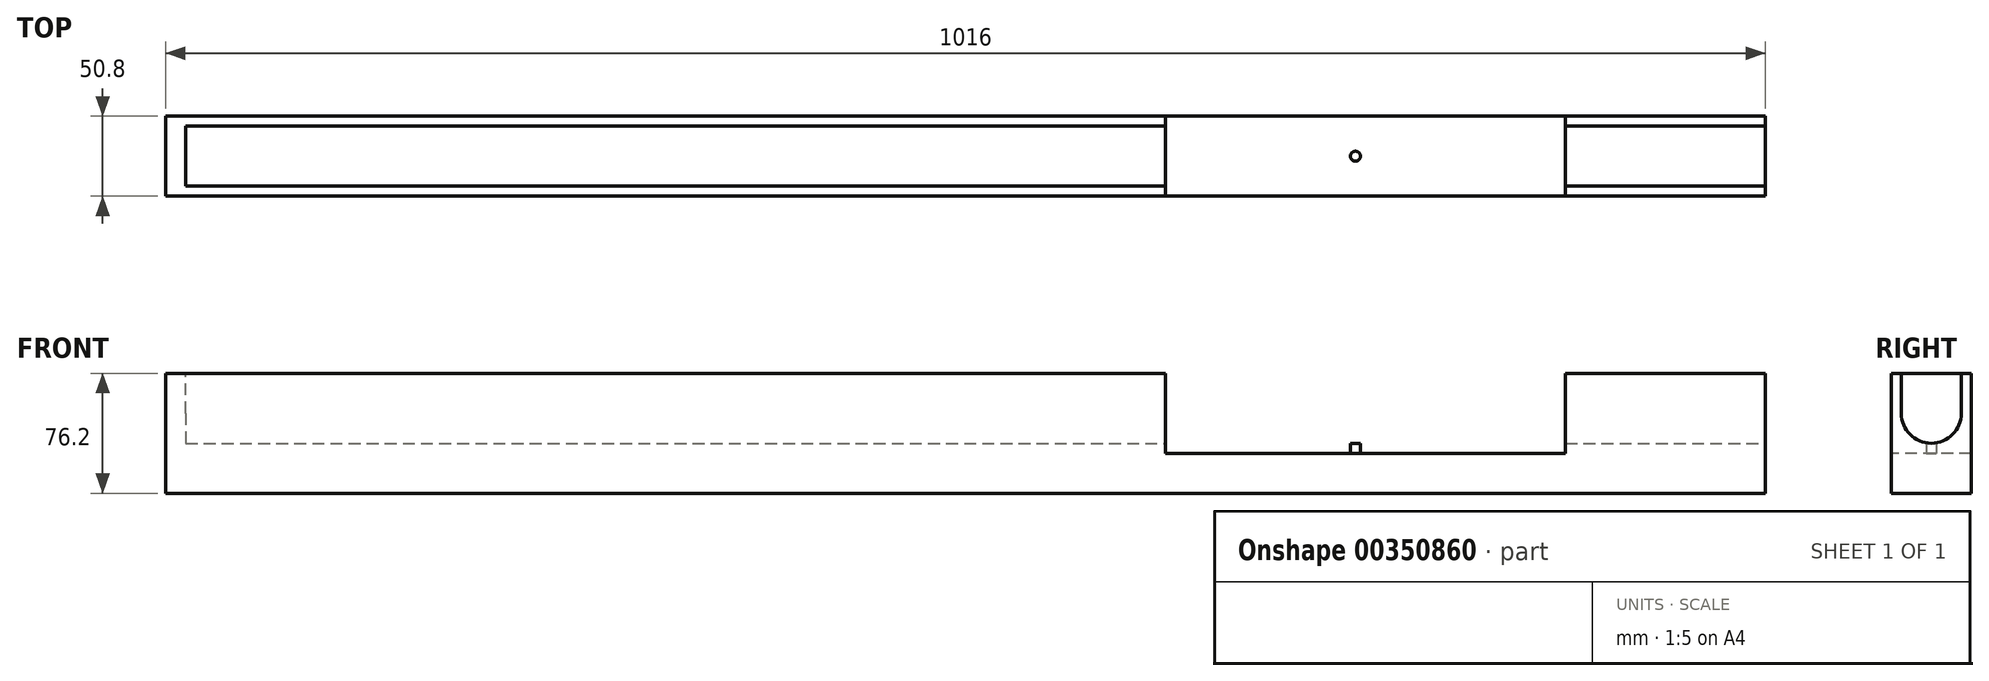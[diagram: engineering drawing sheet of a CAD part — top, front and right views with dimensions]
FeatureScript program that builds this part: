
annotation { "Feature Type Name" : "Feature", "Feature Type Description" : "" }
export const myFeature = defineFeature(function(context is Context, id is Id, definition is map)
    precondition{}
    {
        {
            var Q0;
            Q0=qCreatedBy(makeId("Front.planeOp"),FACE);
            var sketch = newSketch(context, id + "F0", { "sketchPlane" : qUnion([Q0])});
            skLineSegment(sketch, "E0", {"start": v(0, 0) * mm, "end": v(0, 76.2) * mm});
            skLineSegment(sketch, "E1", {"start": v(0, 76.2) * mm, "end": v(254, 76.2) * mm});
            skLineSegment(sketch, "E2", {"start": v(254, 76.2) * mm, "end": v(254, 25.4) * mm});
            skLineSegment(sketch, "E3", {"start": v(254, 25.4) * mm, "end": v(508, 25.4) * mm});
            skLineSegment(sketch, "E4", {"start": v(635, 0) * mm, "end": v(0, 0) * mm});
            skLineSegment(sketch, "E5", {"start": v(508, 25.4) * mm, "end": v(508, 76.2) * mm});
            skLineSegment(sketch, "E6", {"start": v(508, 76.2) * mm, "end": v(635, 76.2) * mm});
            skLineSegment(sketch, "E7", {"start": v(635, 76.2) * mm, "end": v(635, 0) * mm});
            skSolve(sketch);
        }
        {
            var Q0;
            Q0 = qSketchRegion(id + "F0", true);
            extrude(context, id + "F1", {"entities" : qUnion([Q0]), "oppositeDirection" : true, "depth" : 50.8 * mm});
        }
        {
            var Q0;
            Q0=makeQuery(id+"F1.opExtrude","SWEPT_FACE",FACE,{"disambiguationData":[OSD([sQuery(id+"F0.wireOp",EDGE,"E0")])]});
            var sketch = newSketch(context, id + "F2", { "sketchPlane" : qUnion([Q0])});
            skLineSegment(sketch, "E8.bottom", {"start": v(-50.8, 0) * mm, "end": v(0, 0) * mm});
            skLineSegment(sketch, "E8.top", {"start": v(-50.8, 76.2) * mm, "end": v(0, 76.2) * mm});
            skLineSegment(sketch, "E8.left", {"start": v(-50.8, 0) * mm, "end": v(-50.8, 76.2) * mm});
            skLineSegment(sketch, "E8.right", {"start": v(0, 0) * mm, "end": v(0, 76.2) * mm});
            skSolve(sketch);
        }
        {
            var Q0;
            Q0 = qSketchRegion(id + "F2", true);
            extrude(context, id + "F3", {"entities" : qUnion([Q0]), "operationType" : NewBodyOperationType.ADD, "depth" : 381 * mm});
        }
        {
            var Q0;
            Q0=makeQuery(id+"F1.opExtrude","SWEPT_FACE",FACE,{"disambiguationData":[OSD([sQuery(id+"F0.wireOp",EDGE,"E2")])]});
            var sketch = newSketch(context, id + "F4", { "sketchPlane" : qUnion([Q0])});
            skPoint(sketch, "E9", {"position": v(25.4, 50.8) * mm});
            skPoint(sketch, "E9.positionSnap0", {"position": v(50.8, 50.8) * mm});
            skPoint(sketch, "E9.positionSnap1", {"position": v(25.4, 76.2) * mm});
            skCircle(sketch, "E10", {"center": v(25.4, 50.8) * mm, "radius": 19.05 * mm});
            skLineSegment(sketch, "E11", {"start": v(6.35, 50.8) * mm, "end": v(6.35, 76.2) * mm});
            skLineSegment(sketch, "E12", {"start": v(44.45, 50.8) * mm, "end": v(44.45, 76.2) * mm});
            skLineSegment(sketch, "E13", {"start": v(44.45, 76.2) * mm, "end": v(6.35, 76.2) * mm});
            skSolve(sketch);
        }
        {
            var Q0;
            Q0 = qSketchRegion(id + "F4", true);
            extrude(context, id + "F5", {"entities" : qUnion([Q0]), "operationType" : NewBodyOperationType.REMOVE, "oppositeDirection" : true, "depth" : 622.3 * mm, "hasSecondDirection" : true, "secondDirectionBound" : SecondDirectionBoundingType.THROUGH_ALL, "secondDirectionOppositeDirection" : false, "secondDirectionDepth" : 25.4 * mm});
        }
        {
            var Q0;
            Q0=makeQuery(id+"F1.opExtrude","SWEPT_FACE",FACE,{"disambiguationData":[OSD([sQuery(id+"F0.wireOp",EDGE,"E3")])]});
            var sketch = newSketch(context, id + "F6", { "sketchPlane" : qUnion([Q0])});
            skPoint(sketch, "E14", {"position": v(374.65, 25.4) * mm});
            skPoint(sketch, "E14.positionSnap0", {"position": v(254, 25.4) * mm});
            skCircle(sketch, "E15", {"center": v(374.65, 25.4) * mm, "radius": 3.18 * mm});
            skSolve(sketch);
        }
        {
            var Q0;
            Q0 = qSketchRegion(id + "F6", true);
            extrude(context, id + "F7", {"entities" : qUnion([Q0]), "depth" : 6.35 * mm});
        }
        {
            var Q0;
            Q0=makeQuery(id+"F1.opExtrude","SWEPT_BODY",BODY,{"disambiguationData":[OSD([sQuery(id+"F0.wireOp",EDGE,"E0"),sQuery(id+"F0.wireOp",EDGE,"E1"),sQuery(id+"F0.wireOp",EDGE,"E2"),sQuery(id+"F0.wireOp",EDGE,"E3"),sQuery(id+"F0.wireOp",EDGE,"E4"),sQuery(id+"F0.wireOp",EDGE,"E5"),sQuery(id+"F0.wireOp",EDGE,"E6"),sQuery(id+"F0.wireOp",EDGE,"E7")])]});
            var Q1;
            Q1=makeQuery(id+"F3.opExtrude","CAP_FACE",FACE,{"disambiguationData":[OSD([sQuery(id+"F2.wireOp",EDGE,"E8.bottom"),sQuery(id+"F2.wireOp",EDGE,"E8.top"),sQuery(id+"F2.wireOp",EDGE,"E8.left"),sQuery(id+"F2.wireOp",EDGE,"E8.right")])],"isStart":false});
            transform(context, id + "F8", {"entities" : qUnion([Q0]), "transformType" : TransformType.TRANSLATION_DISTANCE, "transformDirection" : qUnion([Q1]), "distance" : 381 * mm, "makeCopy" : false});
        }
        {
            var Q0;
            Q0=makeQuery(id+"F7.opExtrude","SWEPT_BODY",BODY,{"disambiguationData":[OSD([sQuery(id+"F6.wireOp",EDGE,"E15")])]});
            var Q1;
            Q1=makeQuery(id+"F3.opExtrude","CAP_FACE",FACE,{"disambiguationData":[OSD([sQuery(id+"F2.wireOp",EDGE,"E8.bottom"),sQuery(id+"F2.wireOp",EDGE,"E8.top"),sQuery(id+"F2.wireOp",EDGE,"E8.left"),sQuery(id+"F2.wireOp",EDGE,"E8.right")])],"isStart":false});
            transform(context, id + "F9", {"entities" : qUnion([Q0]), "transformType" : TransformType.TRANSLATION_DISTANCE, "transformDirection" : qUnion([Q1]), "distance" : 381 * mm, "makeCopy" : false});
        }
    });
